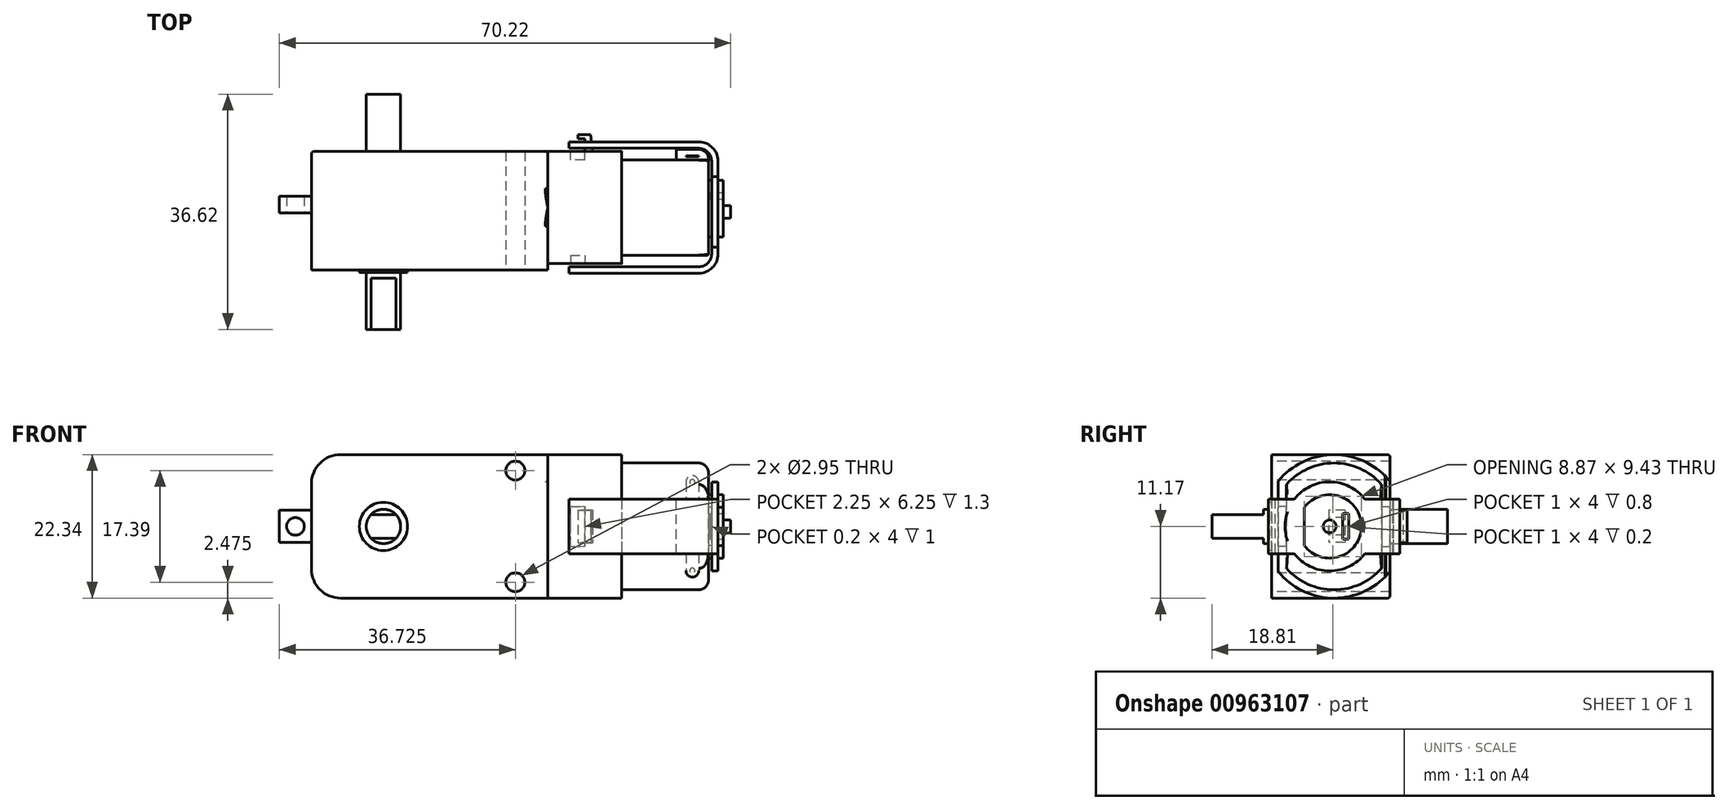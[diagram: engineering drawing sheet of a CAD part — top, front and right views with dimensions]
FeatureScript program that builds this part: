
annotation { "Feature Type Name" : "Feature", "Feature Type Description" : "" }
export const myFeature = defineFeature(function(context is Context, id is Id, definition is map)
    precondition{}
    {
        {
            var Q0;
            Q0=qCreatedBy(makeId("Front.planeOp"),FACE);
            var sketch = newSketch(context, id + "F0", { "sketchPlane" : qUnion([Q0])});
            skCircle(sketch, "E0", {"center": v(0, 0) * mm, "radius": 2.68 * mm});
            skSolve(sketch);
        }
        {
            var Q0;
            Q0 = qSketchRegion(id + "F0", true);
            extrude(context, id + "F1", {"entities" : qUnion([Q0]), "depth" : 36.62 * mm, "offsetDistance" : 25 * mm, "symmetric" : true});
        }
        {
            var Q0;
            Q0=makeQuery(id+"F1.opExtrude","CAP_FACE",FACE,{"disambiguationData":[OSD([sQuery(id+"F0.wireOp",EDGE,"E0")])],"isStart":false});
            var sketch = newSketch(context, id + "F2", { "sketchPlane" : qUnion([Q0])});
            skLineSegment(sketch, "E1.bottom", {"start": v(-5, 6.85) * mm, "end": v(5, 6.85) * mm});
            skLineSegment(sketch, "E1.top", {"start": v(-5, 1.85) * mm, "end": v(5, 1.85) * mm});
            skLineSegment(sketch, "E1.left", {"start": v(-5, 6.85) * mm, "end": v(-5, 1.85) * mm});
            skLineSegment(sketch, "E1.right", {"start": v(5, 6.85) * mm, "end": v(5, 1.85) * mm});
            skLineSegment(sketch, "E2.bottom", {"start": v(-5, -1.85) * mm, "end": v(5, -1.85) * mm});
            skLineSegment(sketch, "E2.top", {"start": v(-5, -6.85) * mm, "end": v(5, -6.85) * mm});
            skLineSegment(sketch, "E2.left", {"start": v(-5, -1.85) * mm, "end": v(-5, -6.85) * mm});
            skLineSegment(sketch, "E2.right", {"start": v(5, -1.85) * mm, "end": v(5, -6.85) * mm});
            skLineSegment(sketch, "E3", {"start": v(0, 1.85) * mm, "end": v(0, -1.85) * mm, "construction": true});
            skSolve(sketch);
        }
        {
            var Q0;
            Q0 = qSketchRegion(id + "F2", true);
            extrude(context, id + "F3", {"entities" : qUnion([Q0]), "operationType" : NewBodyOperationType.REMOVE, "oppositeDirection" : true, "depth" : 8 * mm, "offsetDistance" : 25 * mm});
        }
        {
            var Q0;
            Q0=qCreatedBy(makeId("Front.planeOp"),FACE);
            var sketch = newSketch(context, id + "F4", { "sketchPlane" : qUnion([Q0])});
            skLineSegment(sketch, "E4.bottom", {"start": v(-11.2, 11.17) * mm, "end": v(25.57, 11.17) * mm});
            skLineSegment(sketch, "E4.top", {"start": v(-11.2, -11.17) * mm, "end": v(25.57, -11.17) * mm});
            skLineSegment(sketch, "E4.left", {"start": v(-11.2, 11.17) * mm, "end": v(-11.2, -11.17) * mm});
            skLineSegment(sketch, "E4.right", {"start": v(25.57, 11.17) * mm, "end": v(25.57, -11.17) * mm});
            skSolve(sketch);
        }
        {
            var Q0;
            Q0 = qSketchRegion(id + "F4", true);
            extrude(context, id + "F5", {"entities" : qUnion([Q0]), "operationType" : NewBodyOperationType.ADD, "depth" : (18.8 / 2) * mm, "offsetDistance" : 25 * mm, "hasSecondDirection" : true, "secondDirectionOppositeDirection" : true, "secondDirectionDepth" : (18.8 / 2) * mm});
        }
        {
            var Q0;
            Q0=makeQuery(id+"F5.opExtrude","SWEPT_EDGE",EDGE,{"disambiguationData":[OSD([sQuery(id+"F4.wireOp",EDGE,"E4.bottom"),sQuery(id+"F4.wireOp",EDGE,"E4.left")])]});
            var Q1;
            Q1=makeQuery(id+"F5.opExtrude","SWEPT_EDGE",EDGE,{"disambiguationData":[OSD([sQuery(id+"F4.wireOp",EDGE,"E4.top"),sQuery(id+"F4.wireOp",EDGE,"E4.left")])]});
            fillet(context, id + "F6", {"entities" : qUnion([Q0, Q1]), "radius" : 4.5 * mm, "tangentPropagation" : true, "allowEdgeOverflow" : false});
        }
        {
            var Q0;
            Q0=makeQuery(id+"F5.opExtrude","CAP_FACE",FACE,{"disambiguationData":[OSD([sQuery(id+"F4.wireOp",EDGE,"E4.bottom"),sQuery(id+"F4.wireOp",EDGE,"E4.top"),sQuery(id+"F4.wireOp",EDGE,"E4.left"),sQuery(id+"F4.wireOp",EDGE,"E4.right")])],"isStart":false});
            var sketch = newSketch(context, id + "F7", { "sketchPlane" : qUnion([Q0])});
            skLineSegment(sketch, "E5.0", {"start": v(-6.7, 11.17) * mm, "end": v(25.57, 11.17) * mm});
            skLineSegment(sketch, "E5.1", {"start": v(-11.2, 6.67) * mm, "end": v(-11.2, -6.67) * mm});
            skArc(sketch, "E5.2", {"start": v(-11.2, -6.67) * mm, "mid": v(-9.88, -9.85) * mm, "end": v(-6.7, -11.17) * mm});
            skArc(sketch, "E5.3", {"start": v(-6.7, 11.17) * mm, "mid": v(-9.88, 9.85) * mm, "end": v(-11.2, 6.67) * mm});
            skLineSegment(sketch, "E5.4", {"start": v(-6.7, -11.17) * mm, "end": v(25.57, -11.17) * mm});
            skLineSegment(sketch, "E5.5", {"start": v(25.57, 11.17) * mm, "end": v(25.57, -11.17) * mm});
            skCircle(sketch, "E6", {"center": v(0, 0) * mm, "radius": 3.75 * mm});
            skSolve(sketch);
        }
        {
            var Q0;
            Q0 = qSketchRegion(id + "F7", true);
            extrude(context, id + "F8", {"entities" : qUnion([Q0]), "operationType" : NewBodyOperationType.REMOVE, "oppositeDirection" : true, "depth" : 0.35 * mm, "offsetDistance" : 25 * mm});
        }
        {
            var Q0;
            Q0=makeQuery(id+"F5.opExtrude","SWEPT_FACE",FACE,{"disambiguationData":[OSD([sQuery(id+"F4.wireOp",EDGE,"E4.right")])]});
            var sketch = newSketch(context, id + "F9", { "sketchPlane" : qUnion([Q0])});
            skArc(sketch, "E7", {"start": v(-8.04, -6.97) * mm, "mid": v(0.68, -11.17) * mm, "end": v(9.4, -6.97) * mm});
            skLineSegment(sketch, "E8", {"start": v(-8.04, 6.97) * mm, "end": v(-8.04, -6.97) * mm});
            skLineSegment(sketch, "E9", {"start": v(9.4, 6.97) * mm, "end": v(9.4, -6.97) * mm});
            skArc(sketch, "E10.trimOffspring", {"start": v(9.4, 6.97) * mm, "mid": v(0.68, 11.17) * mm, "end": v(-8.04, 6.97) * mm});
            skSolve(sketch);
        }
        {
            var Q0;
            Q0 = qSketchRegion(id + "F9", true);
            extrude(context, id + "F10", {"entities" : qUnion([Q0]), "operationType" : NewBodyOperationType.ADD, "depth" : 11.5 * mm, "offsetDistance" : 25 * mm});
        }
        {
            var Q0;
            Q0=makeQuery(id+"F10.opExtrude","CAP_FACE",FACE,{"disambiguationData":[OSD([sQuery(id+"F9.wireOp",EDGE,"E7"),sQuery(id+"F9.wireOp",EDGE,"E8"),sQuery(id+"F9.wireOp",EDGE,"E9"),sQuery(id+"F9.wireOp",EDGE,"E10.trimOffspring")])],"isStart":false});
            var sketch = newSketch(context, id + "F11", { "sketchPlane" : qUnion([Q0])});
            skLineSegment(sketch, "E11.0", {"start": v(-6.74, 6.5) * mm, "end": v(-6.74, -6.5) * mm});
            skArc(sketch, "E11.1", {"start": v(8.1, 6.5) * mm, "mid": v(0.68, 9.87) * mm, "end": v(-6.74, 6.5) * mm});
            skLineSegment(sketch, "E11.2", {"start": v(8.1, 6.5) * mm, "end": v(8.1, 4.25) * mm});
            skArc(sketch, "E11.3", {"start": v(-6.75, -6.5) * mm, "mid": v(0.68, -9.87) * mm, "end": v(8.1, -6.5) * mm});
            skLineSegment(sketch, "E12", {"start": v(8.1, 4.25) * mm, "end": v(9.76, 4.25) * mm});
            skLineSegment(sketch, "E13", {"start": v(9.76, 4.25) * mm, "end": v(9.76, -4.25) * mm});
            skLineSegment(sketch, "E14", {"start": v(9.76, -4.25) * mm, "end": v(8.1, -4.25) * mm});
            skLineSegment(sketch, "E15.trimOffspring", {"start": v(8.1, -4.25) * mm, "end": v(8.1, -6.5) * mm});
            skLineSegment(sketch, "E16", {"start": v(0.68, 0) * mm, "end": v(9.76, 0) * mm});
            skSolve(sketch);
        }
        {
            var Q0;
            Q0 = qSketchRegion(id + "F11", true);
            extrude(context, id + "F12", {"entities" : qUnion([Q0]), "operationType" : NewBodyOperationType.ADD, "depth" : 13.5 * mm, "offsetDistance" : 25 * mm});
        }
        {
            var Q0;
            Q0=makeQuery(id+"F12.opExtrude","CAP_FACE",FACE,{"disambiguationData":[OSD([sQuery(id+"F11.wireOp",EDGE,"E11.0"),sQuery(id+"F11.wireOp",EDGE,"E11.1"),sQuery(id+"F11.wireOp",EDGE,"E11.2"),sQuery(id+"F11.wireOp",EDGE,"E11.3")])],"isStart":false});
            var sketch = newSketch(context, id + "F13", { "sketchPlane" : qUnion([Q0])});
            skArc(sketch, "E17", {"start": v(-3.93, -2.98) * mm, "mid": v(4.93, 0) * mm, "end": v(-3.93, 2.98) * mm});
            skLineSegment(sketch, "E18", {"start": v(-3.94, 2.98) * mm, "end": v(-3.94, -2.98) * mm});
            skSolve(sketch);
        }
        {
            var Q0;
            Q0 = qSketchRegion(id + "F13", true);
            extrude(context, id + "F14", {"entities" : qUnion([Q0]), "operationType" : NewBodyOperationType.ADD, "depth" : 2.3 * mm, "offsetDistance" : 25 * mm});
        }
        {
            var Q0;
            Q0=makeQuery(id+"F14.opExtrude","CAP_FACE",FACE,{"disambiguationData":[OSD([sQuery(id+"F13.wireOp",EDGE,"E17"),sQuery(id+"F13.wireOp",EDGE,"E18")])],"isStart":false});
            var sketch = newSketch(context, id + "F15", { "sketchPlane" : qUnion([Q0])});
            skCircle(sketch, "E19", {"center": v(0, 0) * mm, "radius": 1 * mm});
            skSolve(sketch);
        }
        {
            var Q0;
            Q0 = qSketchRegion(id + "F15", true);
            extrude(context, id + "F16", {"entities" : qUnion([Q0]), "operationType" : NewBodyOperationType.ADD, "depth" : 1.15 * mm, "offsetDistance" : 25 * mm});
        }
        {
            var Q0;
            Q0=makeQuery(id+"F14.opExtrude","CAP_FACE",FACE,{"disambiguationData":[OSD([sQuery(id+"F13.wireOp",EDGE,"E17"),sQuery(id+"F13.wireOp",EDGE,"E18")])],"isStart":false});
            var sketch = newSketch(context, id + "F17", { "sketchPlane" : qUnion([Q0])});
            skLineSegment(sketch, "E20.bottom", {"start": v(2, 2) * mm, "end": v(3, 2) * mm});
            skLineSegment(sketch, "E20.top", {"start": v(2, -2) * mm, "end": v(3, -2) * mm});
            skLineSegment(sketch, "E20.left", {"start": v(2, 2) * mm, "end": v(2, -2) * mm});
            skLineSegment(sketch, "E20.right", {"start": v(3, 2) * mm, "end": v(3, -2) * mm});
            skLineSegment(sketch, "E21", {"start": v(0, 0) * mm, "end": v(2, 0) * mm});
            skSolve(sketch);
        }
        {
            var Q0;
            Q0 = qSketchRegion(id + "F17", true);
            extrude(context, id + "F18", {"entities" : qUnion([Q0]), "operationType" : NewBodyOperationType.REMOVE, "oppositeDirection" : true, "depth" : 2 * mm, "offsetDistance" : 25 * mm});
        }
        {
            var Q0;
            Q0=makeQuery(id+"F12.opExtrude","SWEPT_FACE",FACE,{"disambiguationData":[OSD([sQuery(id+"F11.wireOp",EDGE,"E13")])]});
            var sketch = newSketch(context, id + "F19", { "sketchPlane" : qUnion([Q0])});
            skLineSegment(sketch, "E22.bottom", {"start": v(-37.07, 4.25) * mm, "end": v(-45.57, 4.25) * mm});
            skLineSegment(sketch, "E22.top", {"start": v(-37.07, -4.25) * mm, "end": v(-45.57, -4.25) * mm});
            skLineSegment(sketch, "E22.left", {"start": v(-37.07, 4.25) * mm, "end": v(-37.07, -4.25) * mm});
            skLineSegment(sketch, "E22.right", {"start": v(-45.57, 4.25) * mm, "end": v(-45.57, -4.25) * mm});
            skSolve(sketch);
        }
        {
            var Q0;
            Q0 = qSketchRegion(id + "F19", true);
            var Q1;
            Q1=makeQuery(id+"F12.opExtrude","SWEPT_FACE",FACE,{"disambiguationData":[OSD([sQuery(id+"F11.wireOp",EDGE,"E11.2")])]});
            extrude(context, id + "F20", {"entities" : qUnion([Q0]), "operationType" : NewBodyOperationType.REMOVE, "endBound" : BoundingType.UP_TO_SURFACE, "oppositeDirection" : true, "depth" : 25 * mm, "endBoundEntityFace" : qUnion([Q1]), "offsetDistance" : 25 * mm});
        }
        {
            var Q0;
            Q0=makeQuery(id+"F12.opExtrude","SWEPT_FACE",FACE,{"disambiguationData":[OSD([sQuery(id+"F11.wireOp",EDGE,"E13")])]});
            cPlane(context, id + "F21", {"entities" : qUnion([Q0]), "cplaneType" : CPlaneType.OFFSET, "offset" : 1 * mm, "oppositeDirection" : true, "width" : 150 * mm, "height" : 150 * mm});
        }
        {
            var Q0;
            Q0=qCreatedBy(id+"F21.planeOp",FACE);
            var sketch = newSketch(context, id + "F22", { "sketchPlane" : qUnion([Q0])});
            skLineSegment(sketch, "E23.left", {"start": v(-47.07, 6.9) * mm, "end": v(-47.07, -6.9) * mm});
            skLineSegment(sketch, "E23.right", {"start": v(-49.07, 6.9) * mm, "end": v(-49.07, -6.9) * mm});
            skArc(sketch, "E24", {"start": v(-47.07, 6.9) * mm, "mid": v(-48.07, 7.9) * mm, "end": v(-49.07, 6.9) * mm});
            skArc(sketch, "E25", {"start": v(-49.07, -6.9) * mm, "mid": v(-48.07, -7.9) * mm, "end": v(-47.07, -6.9) * mm});
            skLineSegment(sketch, "E26", {"start": v(-48.07, 6.9) * mm, "end": v(-48.07, 4.25) * mm, "construction": true});
            skCircle(sketch, "E27", {"center": v(-48.07, 6.9) * mm, "radius": 0.4 * mm});
            skCircle(sketch, "E28", {"center": v(-48.07, -6.9) * mm, "radius": 0.4 * mm});
            skSolve(sketch);
        }
        {
            var Q0;
            Q0 = qSketchRegion(id + "F22", true);
            extrude(context, id + "F23", {"entities" : qUnion([Q0]), "operationType" : NewBodyOperationType.ADD, "oppositeDirection" : true, "depth" : 0.15 * mm, "offsetDistance" : 25 * mm});
        }
        {
            var Q0;
            Q0=qCreatedBy(makeId("Top.planeOp"),FACE);
            var sketch = newSketch(context, id + "F24", { "sketchPlane" : qUnion([Q0])});
            skLineSegment(sketch, "E29", {"start": v(32.57, 9.4) * mm, "end": v(32.24, 12.04) * mm});
            skLineSegment(sketch, "E30", {"start": v(32.24, 12.04) * mm, "end": v(30.3, 12.04) * mm});
            skLineSegment(sketch, "E31", {"start": v(30.3, 12.04) * mm, "end": v(30.3, 11.4) * mm});
            skLineSegment(sketch, "E32", {"start": v(30.3, 11.4) * mm, "end": v(31.35, 11.4) * mm});
            skLineSegment(sketch, "E33", {"start": v(31.35, 11.4) * mm, "end": v(31.35, 9.4) * mm});
            skLineSegment(sketch, "E34", {"start": v(31.35, 9.4) * mm, "end": v(32.57, 9.4) * mm});
            skSolve(sketch);
        }
        {
            var Q0;
            Q0 = qSketchRegion(id + "F24", true);
            extrude(context, id + "F25", {"entities" : qUnion([Q0]), "operationType" : NewBodyOperationType.ADD, "depth" : 5.05 * mm, "offsetDistance" : 25 * mm, "symmetric" : true});
        }
        {
            var Q0;
            Q0=makeQuery(id+"F10.boolean.opBoolean","MERGE",FACE,{"derivedFrom":[makeQuery(id+"F5.opExtrude","CAP_FACE",FACE,{"disambiguationData":[OSD([sQuery(id+"F4.wireOp",EDGE,"E4.bottom"),sQuery(id+"F4.wireOp",EDGE,"E4.top"),sQuery(id+"F4.wireOp",EDGE,"E4.left"),sQuery(id+"F4.wireOp",EDGE,"E4.right")])],"isStart":true}),makeQuery(id+"F10.opExtrude","SWEPT_FACE",FACE,{"disambiguationData":[OSD([sQuery(id+"F9.wireOp",EDGE,"E9")])]})]});
            cPlane(context, id + "F26", {"entities" : qUnion([Q0]), "cplaneType" : CPlaneType.OFFSET, "offset" : (17.45 / 2) * mm, "oppositeDirection" : true, "width" : 150 * mm, "height" : 150 * mm});
        }
        {
            var Q0;
            Q0=makeQuery(id+"F10.boolean.opBoolean","MERGE",FACE,{"derivedFrom":[makeQuery(id+"F5.opExtrude","CAP_FACE",FACE,{"disambiguationData":[OSD([sQuery(id+"F4.wireOp",EDGE,"E4.bottom"),sQuery(id+"F4.wireOp",EDGE,"E4.top"),sQuery(id+"F4.wireOp",EDGE,"E4.left"),sQuery(id+"F4.wireOp",EDGE,"E4.right")])],"isStart":true}),makeQuery(id+"F10.opExtrude","SWEPT_FACE",FACE,{"disambiguationData":[OSD([sQuery(id+"F9.wireOp",EDGE,"E9")])]})]});
            var sketch = newSketch(context, id + "F27", { "sketchPlane" : qUnion([Q0])});
            skLineSegment(sketch, "E35.bottom", {"start": v(-29.1, -3.12) * mm, "end": v(-31.35, -3.12) * mm});
            skLineSegment(sketch, "E35.top", {"start": v(-29.1, 3.12) * mm, "end": v(-31.35, 3.12) * mm});
            skLineSegment(sketch, "E35.left", {"start": v(-29.1, -3.12) * mm, "end": v(-29.1, 3.12) * mm});
            skLineSegment(sketch, "E35.right", {"start": v(-31.35, -3.12) * mm, "end": v(-31.35, 3.12) * mm});
            skPoint(sketch, "E36", {"position": v(-31.35, 0) * mm});
            skSolve(sketch);
        }
        {
            var Q0;
            Q0 = qSketchRegion(id + "F27", true);
            var Q1;
            Q1=makeQuery(id+"F20.boolean.opBoolean","MERGE",FACE,{"derivedFrom":[makeQuery(id+"F12.opExtrude","SWEPT_FACE",FACE,{"disambiguationData":[OSD([sQuery(id+"F11.wireOp",EDGE,"E11.2")])]}),makeQuery(id+"F12.opExtrude","SWEPT_FACE",FACE,{"disambiguationData":[OSD([sQuery(id+"F11.wireOp",EDGE,"E15.trimOffspring")])]})],"fromTools":[makeQuery(id+"F20.opExtrude","CAP_FACE",FACE,{"disambiguationData":[OSD([sQuery(id+"F19.wireOp",EDGE,"E22.bottom"),sQuery(id+"F19.wireOp",EDGE,"E22.top"),sQuery(id+"F19.wireOp",EDGE,"E22.left"),sQuery(id+"F19.wireOp",EDGE,"E22.right")])],"isStart":false})]});
            extrude(context, id + "F28", {"entities" : qUnion([Q0]), "operationType" : NewBodyOperationType.REMOVE, "endBound" : BoundingType.UP_TO_SURFACE, "oppositeDirection" : true, "depth" : 25 * mm, "endBoundEntityFace" : qUnion([Q1]), "offsetDistance" : 25 * mm});
        }
        {
            var Q0;
            Q0=makeQuery(id+"F10.opExtrude","SWEPT_FACE",FACE,{"disambiguationData":[OSD([sQuery(id+"F9.wireOp",EDGE,"E8")])]});
            var sketch = newSketch(context, id + "F29", { "sketchPlane" : qUnion([Q0])});
            skLineSegment(sketch, "E37.0", {"start": v(29.1, 3.12) * mm, "end": v(31.35, 3.12) * mm});
            skLineSegment(sketch, "E37.1", {"start": v(29.1, -3.12) * mm, "end": v(29.1, 3.12) * mm});
            skLineSegment(sketch, "E37.2", {"start": v(31.35, -3.12) * mm, "end": v(31.35, 3.12) * mm});
            skLineSegment(sketch, "E37.3", {"start": v(29.1, -3.12) * mm, "end": v(31.35, -3.12) * mm});
            skSolve(sketch);
        }
        {
            var Q0;
            Q0 = qSketchRegion(id + "F29", true);
            var Q1;
            Q1=makeQuery(id+"F12.opExtrude","SWEPT_FACE",FACE,{"disambiguationData":[OSD([sQuery(id+"F11.wireOp",EDGE,"E11.0")])]});
            extrude(context, id + "F30", {"entities" : qUnion([Q0]), "operationType" : NewBodyOperationType.REMOVE, "endBound" : BoundingType.UP_TO_SURFACE, "oppositeDirection" : true, "depth" : 25 * mm, "endBoundEntityFace" : qUnion([Q1]), "offsetDistance" : 25 * mm});
        }
        {
            var Q0;
            Q0=makeQuery(id+"F12.opExtrude","CAP_EDGE",EDGE,{"disambiguationData":[OSD([sQuery(id+"F11.wireOp",EDGE,"E11.3")])],"isStart":false});
            var Q1;
            Q1=makeQuery(id+"F12.opExtrude","CAP_EDGE",EDGE,{"disambiguationData":[OSD([sQuery(id+"F11.wireOp",EDGE,"E11.1")])],"isStart":false});
            var Q2;
            Q2=makeQuery(id+"F12.opExtrude","CAP_EDGE",EDGE,{"disambiguationData":[OSD([sQuery(id+"F11.wireOp",EDGE,"E13")])],"isStart":false});
            fillet(context, id + "F31", {"entities" : qUnion([Q0, Q1, Q2]), "radius" : 1.5 * mm, "tangentPropagation" : true, "allowEdgeOverflow" : false});
        }
        {
            var Q0;
            Q0=qCreatedBy(makeId("Top.planeOp"),FACE);
            var sketch = newSketch(context, id + "F32", { "sketchPlane" : qUnion([Q0])});
            skLineSegment(sketch, "E38", {"start": v(28.85, -8.54) * mm, "end": v(28.85, -9.54) * mm});
            skLineSegment(sketch, "E39", {"start": v(28.85, -9.54) * mm, "end": v(49.07, -9.54) * mm});
            skLineSegment(sketch, "E40", {"start": v(52.07, -6.54) * mm, "end": v(52.07, 7.9) * mm});
            skLineSegment(sketch, "E41", {"start": v(49.07, 10.9) * mm, "end": v(28.85, 10.9) * mm});
            skLineSegment(sketch, "E42", {"start": v(28.85, 10.9) * mm, "end": v(28.85, 9.9) * mm});
            skLineSegment(sketch, "E43", {"start": v(28.85, 9.9) * mm, "end": v(49.07, 9.9) * mm});
            skLineSegment(sketch, "E44", {"start": v(51.07, 7.9) * mm, "end": v(51.07, -6.54) * mm});
            skLineSegment(sketch, "E45", {"start": v(49.07, -8.54) * mm, "end": v(28.85, -8.54) * mm});
            skPoint(sketch, "E46.visualSharp", {"position": v(51.07, -8.54) * mm});
            skArc(sketch, "E46.filletArc", {"start": v(49.07, -8.54) * mm, "mid": v(50.48, -7.96) * mm, "end": v(51.07, -6.54) * mm});
            skPoint(sketch, "E47.visualSharp", {"position": v(51.07, 9.9) * mm});
            skArc(sketch, "E47.filletArc", {"start": v(51.07, 7.9) * mm, "mid": v(50.48, 9.32) * mm, "end": v(49.07, 9.9) * mm});
            skPoint(sketch, "E48.visualSharp", {"position": v(52.07, -9.54) * mm});
            skArc(sketch, "E48.filletArc", {"start": v(49.07, -9.54) * mm, "mid": v(51.2, -8.67) * mm, "end": v(52.07, -6.54) * mm});
            skPoint(sketch, "E49.visualSharp", {"position": v(52.07, 10.9) * mm});
            skArc(sketch, "E49.filletArc", {"start": v(52.07, 7.9) * mm, "mid": v(51.2, 10.03) * mm, "end": v(49.07, 10.9) * mm});
            skSolve(sketch);
        }
        {
            var Q0;
            Q0 = qSketchRegion(id + "F32", true);
            extrude(context, id + "F33", {"entities" : qUnion([Q0]), "operationType" : NewBodyOperationType.ADD, "depth" : 8.5 * mm, "offsetDistance" : 25 * mm, "symmetric" : true});
        }
        {
            var Q0;
            {var subQ0=sQuery(id+"F32.wireOp",EDGE,"E49.filletArc");var subQ9=sQuery(id+"F32.wireOp",EDGE,"E40");Q0=makeQuery(id+"F33.boolean.opBoolean","SPLIT",FACE,{"disambiguationData":[TD([makeQuery(id+"F33.opExtrude","SWEPT_FACE",FACE,{"disambiguationData":[OSD([subQ0])]})])],"derivedFrom":makeQuery(id+"F33.opExtrude","SWEPT_FACE",FACE,{"disambiguationData":[OSD([subQ9])]})});}
            var sketch = newSketch(context, id + "F34", { "sketchPlane" : qUnion([Q0])});
            skCircle(sketch, "E50", {"center": v(0, 0) * mm, "radius": 6.94 * mm});
            skSolve(sketch);
        }
        {
            var Q0;
            Q0 = qSketchRegion(id + "F34", true);
            var Q1;
            {var subQ5=sQuery(id+"F32.wireOp",EDGE,"E44");Q1=makeQuery(id+"F33.boolean.opBoolean","SPLIT",FACE,{"disambiguationData":[TD([makeQuery(id+"F14.opExtrude","SWEPT_FACE",FACE,{"disambiguationData":[OSD([sQuery(id+"F13.wireOp",EDGE,"E18")])]})])],"derivedFrom":makeQuery(id+"F33.opExtrude","SWEPT_FACE",FACE,{"disambiguationData":[OSD([subQ5])]})});}
            extrude(context, id + "F35", {"entities" : qUnion([Q0]), "operationType" : NewBodyOperationType.ADD, "endBound" : BoundingType.UP_TO_SURFACE, "oppositeDirection" : true, "depth" : 25 * mm, "endBoundEntityFace" : qUnion([Q1]), "offsetDistance" : 25 * mm});
        }
        {
            var Q0;
            Q0=makeQuery(id+"F8.boolean.opBoolean","COPY",FACE,{"derivedFrom":makeQuery(id+"F8.opExtrude","CAP_FACE",FACE,{"disambiguationData":[OSD([sQuery(id+"F7.wireOp",EDGE,"E5.0"),sQuery(id+"F7.wireOp",EDGE,"E5.1"),sQuery(id+"F7.wireOp",EDGE,"E5.2"),sQuery(id+"F7.wireOp",EDGE,"E5.3"),sQuery(id+"F7.wireOp",EDGE,"E5.4"),sQuery(id+"F7.wireOp",EDGE,"E5.5"),sQuery(id+"F7.wireOp",EDGE,"E6")])],"isStart":false})});
            cPlane(context, id + "F36", {"entities" : qUnion([Q0]), "cplaneType" : CPlaneType.OFFSET, "offset" : 8.9 * mm, "oppositeDirection" : true, "width" : 150 * mm, "height" : 150 * mm});
        }
        {
            var Q0;
            Q0=qCreatedBy(id+"F36.planeOp",FACE);
            var sketch = newSketch(context, id + "F37", { "sketchPlane" : qUnion([Q0])});
            skLineSegment(sketch, "E51.bottom", {"start": v(-16.2, 2.5) * mm, "end": v(-11.2, 2.5) * mm});
            skLineSegment(sketch, "E51.top", {"start": v(-16.2, -2.5) * mm, "end": v(-11.2, -2.5) * mm});
            skLineSegment(sketch, "E51.left", {"start": v(-16.2, 2.5) * mm, "end": v(-16.2, -2.5) * mm});
            skLineSegment(sketch, "E51.right", {"start": v(-11.2, 2.5) * mm, "end": v(-11.2, -2.5) * mm});
            skLineSegment(sketch, "E52", {"start": v(-11.2, 0) * mm, "end": v(0, 0) * mm, "construction": true});
            skPoint(sketch, "E52.startSnap0", {"position": v(-11.2, 0) * mm});
            skCircle(sketch, "E53", {"center": v(-13.7, 0) * mm, "radius": 1.38 * mm});
            skSolve(sketch);
        }
        {
            var Q0;
            Q0 = qSketchRegion(id + "F37", true);
            extrude(context, id + "F38", {"entities" : qUnion([Q0]), "operationType" : NewBodyOperationType.ADD, "oppositeDirection" : true, "depth" : 2.57 * mm, "offsetDistance" : 25 * mm});
        }
        {
            var Q0;
            Q0=makeQuery(id+"F8.boolean.opBoolean","COPY",FACE,{"derivedFrom":makeQuery(id+"F8.opExtrude","CAP_FACE",FACE,{"disambiguationData":[OSD([sQuery(id+"F7.wireOp",EDGE,"E5.0"),sQuery(id+"F7.wireOp",EDGE,"E5.1"),sQuery(id+"F7.wireOp",EDGE,"E5.2"),sQuery(id+"F7.wireOp",EDGE,"E5.3"),sQuery(id+"F7.wireOp",EDGE,"E5.4"),sQuery(id+"F7.wireOp",EDGE,"E5.5"),sQuery(id+"F7.wireOp",EDGE,"E6")])],"isStart":false})});
            var sketch = newSketch(context, id + "F39", { "sketchPlane" : qUnion([Q0])});
            skCircle(sketch, "E54", {"center": v(20.53, -8.7) * mm, "radius": 1.47 * mm});
            skCircle(sketch, "E55", {"center": v(20.53, 8.7) * mm, "radius": 1.48 * mm});
            skSolve(sketch);
        }
        {
            var Q0;
            Q0 = qSketchRegion(id + "F39", true);
            extrude(context, id + "F40", {"entities" : qUnion([Q0]), "operationType" : NewBodyOperationType.REMOVE, "endBound" : BoundingType.UP_TO_NEXT, "oppositeDirection" : true, "depth" : 25 * mm, "offsetDistance" : 25 * mm});
        }
        {
            var Q0;
            Q0=makeQuery(id+"F8.boolean.opBoolean","COPY",EDGE,{"derivedFrom":makeQuery(id+"F8.opExtrude","CAP_EDGE",EDGE,{"disambiguationData":[OSD([sQuery(id+"F7.wireOp",EDGE,"E5.0")])],"isStart":false})});
            var Q1;
            Q1=makeQuery(id+"F5.opExtrude","CAP_EDGE",EDGE,{"disambiguationData":[OSD([sQuery(id+"F4.wireOp",EDGE,"E4.bottom")])],"isStart":true});
            fillet(context, id + "F41", {"entities" : qUnion([Q0, Q1]), "radius" : 0.4 * mm, "tangentPropagation" : true, "allowEdgeOverflow" : false});
        }
        {
            var Q0;
            {var subQ0=sQuery(id+"F4.wireOp",EDGE,"E4.bottom");var subQ1=sQuery(id+"F4.wireOp",EDGE,"E4.right");Q0=makeQuery(id+"F10.boolean.opBoolean","SPLIT",EDGE,{"disambiguationData":[TD([makeQuery(id+"F8.boolean.opBoolean","COPY",FACE,{"derivedFrom":makeQuery(id+"F8.opExtrude","CAP_FACE",FACE,{"disambiguationData":[OSD([sQuery(id+"F7.wireOp",EDGE,"E5.0"),sQuery(id+"F7.wireOp",EDGE,"E5.1"),sQuery(id+"F7.wireOp",EDGE,"E5.2"),sQuery(id+"F7.wireOp",EDGE,"E5.3"),sQuery(id+"F7.wireOp",EDGE,"E5.4"),sQuery(id+"F7.wireOp",EDGE,"E5.5"),sQuery(id+"F7.wireOp",EDGE,"E6")])],"isStart":false})})])],"derivedFrom":makeQuery(id+"F5.opExtrude","SWEPT_EDGE",EDGE,{"disambiguationData":[OSD([subQ0,subQ1])]})});}
            var Q1;
            Q1=makeQuery(id+"F10.opExtrude","SWEPT_EDGE",EDGE,{"disambiguationData":[OSD([sQuery(id+"F9.wireOp",EDGE,"E8"),sQuery(id+"F9.wireOp",EDGE,"E10.trimOffspring")])]});
            var Q2;
            Q2=makeQuery(id+"F10.opExtrude","SWEPT_EDGE",EDGE,{"disambiguationData":[OSD([sQuery(id+"F9.wireOp",EDGE,"E7"),sQuery(id+"F9.wireOp",EDGE,"E8")])]});
            var Q3;
            Q3=makeQuery(id+"F10.opExtrude","SWEPT_EDGE",EDGE,{"disambiguationData":[OSD([sQuery(id+"F4.wireOp",EDGE,"E4.right"),sQuery(id+"F9.wireOp",EDGE,"E9"),sQuery(id+"F9.wireOp",EDGE,"E10.trimOffspring")])]});
            var Q4;
            Q4=makeQuery(id+"F10.opExtrude","SWEPT_EDGE",EDGE,{"disambiguationData":[OSD([sQuery(id+"F4.wireOp",EDGE,"E4.right"),sQuery(id+"F9.wireOp",EDGE,"E7"),sQuery(id+"F9.wireOp",EDGE,"E9")])]});
            fillet(context, id + "F42", {"entities" : qUnion([Q0, Q1, Q2, Q3, Q4]), "radius" : 0.4 * mm, "tangentPropagation" : true, "allowEdgeOverflow" : false});
        }
        {
            var Q0;
            Q0=makeQuery(id+"F12.opExtrude","SWEPT_EDGE",EDGE,{"disambiguationData":[OSD([sQuery(id+"F11.wireOp",EDGE,"E11.0"),sQuery(id+"F11.wireOp",EDGE,"E11.1")])]});
            var Q1;
            Q1=makeQuery(id+"F12.opExtrude","SWEPT_EDGE",EDGE,{"disambiguationData":[OSD([sQuery(id+"F11.wireOp",EDGE,"E11.1"),sQuery(id+"F11.wireOp",EDGE,"E11.2")])]});
            var Q2;
            Q2=makeQuery(id+"F12.opExtrude","SWEPT_EDGE",EDGE,{"disambiguationData":[OSD([sQuery(id+"F11.wireOp",EDGE,"E11.3"),sQuery(id+"F11.wireOp",EDGE,"E15.trimOffspring")])]});
            fillet(context, id + "F43", {"entities" : qUnion([Q0, Q1, Q2]), "radius" : 0.2 * mm, "tangentPropagation" : true, "allowEdgeOverflow" : false});
        }
    });
